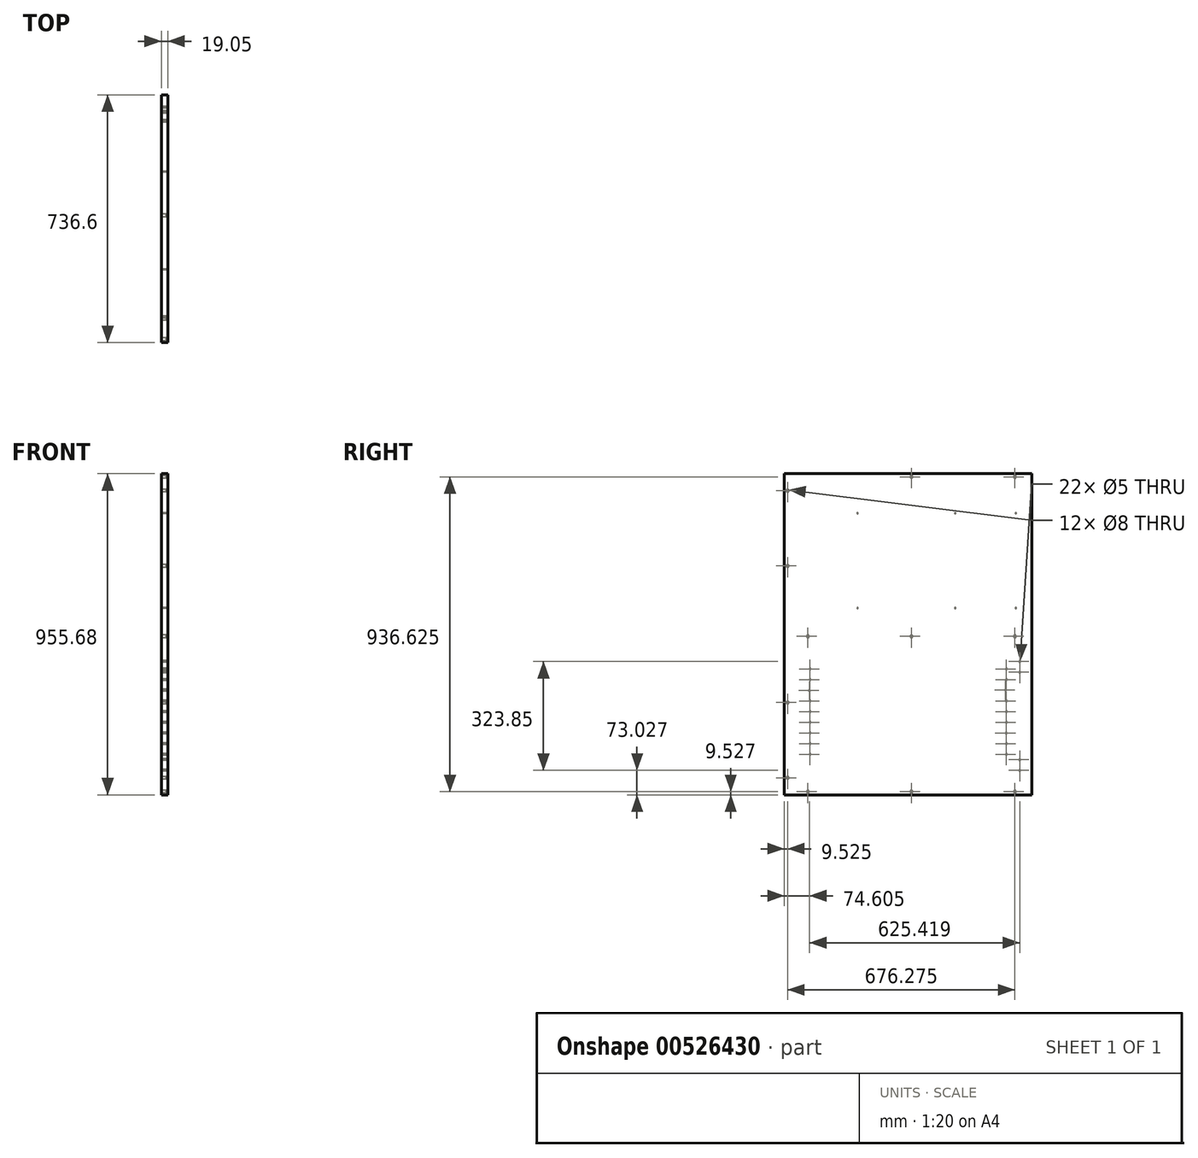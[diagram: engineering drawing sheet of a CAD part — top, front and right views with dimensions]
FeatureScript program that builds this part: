
annotation { "Feature Type Name" : "Feature", "Feature Type Description" : "" }
export const myFeature = defineFeature(function(context is Context, id is Id, definition is map)
    precondition{}
    {
        {
            var Q0;
            Q0=qCreatedBy(makeId("Right.planeOp"),FACE);
            var sketch = newSketch(context, id + "F0", { "sketchPlane" : qUnion([Q0])});
            skLineSegment(sketch, "E0.bottom", {"start": v(368.3, 477.84) * mm, "end": v(-368.3, 477.84) * mm});
            skLineSegment(sketch, "E0.top", {"start": v(368.3, -477.84) * mm, "end": v(-368.3, -477.84) * mm});
            skLineSegment(sketch, "E0.left", {"start": v(368.3, 477.84) * mm, "end": v(368.3, -477.84) * mm});
            skLineSegment(sketch, "E0.right", {"start": v(-368.3, 477.84) * mm, "end": v(-368.3, -477.84) * mm});
            skPoint(sketch, "E0.middle", {"position": v(0, 0) * mm});
            skSolve(sketch);
        }
        {
            var Q0;
            Q0=makeQuery(id+"F0.imprint","IMPRINT",FACE,{"disambiguationData":[TD([[makeQuery(id+"F0.imprint","IMPRINT",EDGE,{"derivedFrom":sQuery(id+"F0.wireOp",EDGE,"E0.bottom")}),1.0]])]});
            extrude(context, id + "F1", {"entities" : qUnion([Q0]), "depth" : 19.05 * mm, "offsetDistance" : 25.4 * mm});
        }
        {
            var Q0;
            Q0=makeQuery(id+"F1.opExtrude","CAP_FACE",FACE,{"disambiguationData":[OSD([sQuery(id+"F0.wireOp",EDGE,"E0.bottom"),sQuery(id+"F0.wireOp",EDGE,"E0.top"),sQuery(id+"F0.wireOp",EDGE,"E0.left"),sQuery(id+"F0.wireOp",EDGE,"E0.right")])],"isStart":false});
            var sketch = newSketch(context, id + "F2", { "sketchPlane" : qUnion([Q0])});
            skLineSegment(sketch, "E1", {"start": v(368.3, 477.84) * mm, "end": v(368.3, 468.31) * mm});
            skLineSegment(sketch, "E2", {"start": v(368.3, 468.31) * mm, "end": v(-368.3, 468.31) * mm});
            skLineSegment(sketch, "E3", {"start": v(-368.3, 477.84) * mm, "end": v(-349.25, 477.84) * mm});
            skLineSegment(sketch, "E4", {"start": v(-349.25, 477.84) * mm, "end": v(-349.25, -477.84) * mm});
            skLineSegment(sketch, "E5", {"start": v(-368.3, -477.84) * mm, "end": v(-368.3, -468.31) * mm});
            skLineSegment(sketch, "E6", {"start": v(-368.3, -468.31) * mm, "end": v(368.3, -468.31) * mm});
            skLineSegment(sketch, "E7", {"start": v(-368.3, -477.84) * mm, "end": v(-358.77, -477.84) * mm});
            skLineSegment(sketch, "E8", {"start": v(-358.77, -477.84) * mm, "end": v(-358.78, 477.84) * mm});
            skLineSegment(sketch, "E9", {"start": v(-368.3, 468.31) * mm, "end": v(-298.45, 468.31) * mm});
            skLineSegment(sketch, "E10", {"start": v(-368.3, -468.31) * mm, "end": v(-298.45, -468.31) * mm});
            skLineSegment(sketch, "E11", {"start": v(368.3, -468.31) * mm, "end": v(317.5, -468.31) * mm});
            skLineSegment(sketch, "E12", {"start": v(368.3, -468.31) * mm, "end": v(9.53, -468.31) * mm});
            skLineSegment(sketch, "E13", {"start": v(-358.78, 477.84) * mm, "end": v(-358.78, 427.04) * mm});
            skLineSegment(sketch, "E14", {"start": v(-358.77, -477.84) * mm, "end": v(-358.77, -427.04) * mm});
            skPoint(sketch, "E15", {"position": v(-358.78, 427.04) * mm});
            skPoint(sketch, "E16", {"position": v(317.5, -468.31) * mm});
            skPoint(sketch, "E17", {"position": v(9.53, -468.31) * mm});
            skPoint(sketch, "E18", {"position": v(-298.45, -468.31) * mm});
            skPoint(sketch, "E19", {"position": v(-358.77, -427.04) * mm});
            skPoint(sketch, "E20", {"position": v(-358.78, 0) * mm});
            skLineSegment(sketch, "E21", {"start": v(-368.3, 468.31) * mm, "end": v(-368.3, 477.84) * mm});
            skLineSegment(sketch, "E22", {"start": v(368.3, 468.31) * mm, "end": v(317.5, 468.31) * mm});
            skLineSegment(sketch, "E23", {"start": v(317.5, 468.31) * mm, "end": v(9.52, 468.31) * mm});
            skLineSegment(sketch, "E24", {"start": v(-358.78, 0) * mm, "end": v(-358.78, 203.2) * mm});
            skLineSegment(sketch, "E25", {"start": v(-358.78, 203.2) * mm, "end": v(-358.77, -203.2) * mm});
            skPoint(sketch, "E26", {"position": v(-358.78, 203.2) * mm});
            skPoint(sketch, "E27", {"position": v(-358.77, -203.2) * mm});
            skSolve(sketch);
        }
        {
            var Q0;
            Q0=sQuery(id+"F2.wireOp",VERTEX,"E9.end");
            var Q1;
            Q1=sQuery(id+"F2.wireOp",VERTEX,"E23.end");
            var Q2;
            Q2=sQuery(id+"F2.wireOp",VERTEX,"E23.start");
            var Q3;
            Q3=sQuery(id+"F2.wireOp",VERTEX,"E15");
            var Q4;
            Q4=sQuery(id+"F2.wireOp",VERTEX,"E19");
            var Q5;
            Q5=sQuery(id+"F2.wireOp",VERTEX,"E18");
            var Q6;
            Q6=sQuery(id+"F2.wireOp",VERTEX,"E17");
            var Q7;
            Q7=sQuery(id+"F2.wireOp",VERTEX,"E16");
            var Q8;
            Q8=sQuery(id+"F2.wireOp",VERTEX,"E26");
            var Q9;
            Q9=sQuery(id+"F2.wireOp",VERTEX,"E27");
            var Q10;
            Q10=makeQuery(id+"F1.opExtrude","SWEPT_BODY",BODY,{"disambiguationData":[OSD([sQuery(id+"F0.wireOp",EDGE,"E0.bottom"),sQuery(id+"F0.wireOp",EDGE,"E0.top"),sQuery(id+"F0.wireOp",EDGE,"E0.left"),sQuery(id+"F0.wireOp",EDGE,"E0.right")])]});
            hole(context, id + "F3", {"style" : HoleStyle.SIMPLE, "endStyle" : HoleEndStyle.BLIND, "holeDiameter" : 8 * mm, "holeDepth" : 14.22 * mm, "isTappedThrough" : true, "tappedDepth" : 12.7 * mm, "tapClearance" : 3, "startFromSketch" : true, "locations" : qUnion([Q0, Q1, Q2, Q3, Q4, Q5, Q6, Q7, Q8, Q9]), "scope" : qUnion([Q10])});
        }
        {
            var Q0;
            Q0=makeQuery(id+"F1.opExtrude","CAP_FACE",FACE,{"disambiguationData":[OSD([sQuery(id+"F0.wireOp",EDGE,"E0.bottom"),sQuery(id+"F0.wireOp",EDGE,"E0.top"),sQuery(id+"F0.wireOp",EDGE,"E0.left"),sQuery(id+"F0.wireOp",EDGE,"E0.right")])],"isStart":false});
            var sketch = newSketch(context, id + "F4", { "sketchPlane" : qUnion([Q0])});
            skLineSegment(sketch, "E28", {"start": v(368.3, 477.84) * mm, "end": v(368.3, 363.54) * mm});
            skLineSegment(sketch, "E29", {"start": v(368.3, 477.84) * mm, "end": v(368.3, 458.79) * mm});
            skLineSegment(sketch, "E30", {"start": v(368.3, 458.79) * mm, "end": v(368.3, 360.24) * mm});
            skLineSegment(sketch, "E31", {"start": v(368.3, 360.24) * mm, "end": v(-241.3, 360.24) * mm});
            skLineSegment(sketch, "E32", {"start": v(368.3, 360.24) * mm, "end": v(320.04, 360.24) * mm});
            skLineSegment(sketch, "E33", {"start": v(368.3, 360.24) * mm, "end": v(139.7, 360.24) * mm});
            skLineSegment(sketch, "E34", {"start": v(368.3, 360.24) * mm, "end": v(-150.88, 360.24) * mm});
            skPoint(sketch, "E35", {"position": v(320.04, 360.24) * mm});
            skPoint(sketch, "E36", {"position": v(139.7, 360.24) * mm});
            skPoint(sketch, "E37", {"position": v(-150.88, 360.24) * mm});
            skLineSegment(sketch, "E38", {"start": v(368.3, 477.84) * mm, "end": v(368.3, 468.31) * mm});
            skLineSegment(sketch, "E39", {"start": v(368.3, 468.31) * mm, "end": v(387.35, 468.31) * mm});
            skLineSegment(sketch, "E40", {"start": v(387.35, 468.31) * mm, "end": v(387.35, 303.21) * mm});
            skLineSegment(sketch, "E41", {"start": v(387.35, 303.21) * mm, "end": v(368.3, 303.21) * mm});
            skLineSegment(sketch, "E42", {"start": v(368.3, 303.21) * mm, "end": v(368.3, 300.04) * mm});
            skLineSegment(sketch, "E43", {"start": v(368.3, 300.04) * mm, "end": v(387.35, 300.04) * mm});
            skLineSegment(sketch, "E44", {"start": v(387.35, 300.04) * mm, "end": v(387.35, 0) * mm});
            skLineSegment(sketch, "E45", {"start": v(387.35, 300.04) * mm, "end": v(387.35, -4.76) * mm});
            skLineSegment(sketch, "E46", {"start": v(387.35, -4.76) * mm, "end": v(368.3, -4.76) * mm});
            skLineSegment(sketch, "E47", {"start": v(368.3, -4.76) * mm, "end": v(368.3, -7.94) * mm});
            skLineSegment(sketch, "E48", {"start": v(368.3, -7.94) * mm, "end": v(387.35, -7.94) * mm});
            skLineSegment(sketch, "E49", {"start": v(387.35, -7.94) * mm, "end": v(387.35, -477.84) * mm});
            skLineSegment(sketch, "E50", {"start": v(387.35, -477.84) * mm, "end": v(368.3, -477.84) * mm});
            skLineSegment(sketch, "E51", {"start": v(387.35, 147.64) * mm, "end": v(387.35, 280.99) * mm});
            skLineSegment(sketch, "E52", {"start": v(387.35, 280.99) * mm, "end": v(311.15, 280.99) * mm});
            skLineSegment(sketch, "E53", {"start": v(311.15, 280.99) * mm, "end": v(311.15, 14.29) * mm});
            skLineSegment(sketch, "E54", {"start": v(311.15, 14.29) * mm, "end": v(387.35, 14.29) * mm});
            skLineSegment(sketch, "E55", {"start": v(368.3, 14.29) * mm, "end": v(368.3, 77.79) * mm});
            skLineSegment(sketch, "E56", {"start": v(368.3, 77.79) * mm, "end": v(-241.3, 77.79) * mm});
            skLineSegment(sketch, "E57", {"start": v(368.3, 77.79) * mm, "end": v(320.04, 77.79) * mm});
            skLineSegment(sketch, "E58", {"start": v(368.3, 77.79) * mm, "end": v(-150.88, 77.79) * mm});
            skLineSegment(sketch, "E59", {"start": v(368.3, 77.79) * mm, "end": v(139.7, 77.79) * mm});
            skPoint(sketch, "E60", {"position": v(139.7, 77.79) * mm});
            skPoint(sketch, "E61", {"position": v(-150.88, 77.79) * mm});
            skPoint(sketch, "E62", {"position": v(320.04, 77.79) * mm});
            skLineSegment(sketch, "E63", {"start": v(368.3, -6.35) * mm, "end": v(-368.3, -6.35) * mm});
            skLineSegment(sketch, "E64", {"start": v(-368.3, -6.35) * mm, "end": v(-298.45, -6.35) * mm});
            skLineSegment(sketch, "E65", {"start": v(368.3, -6.35) * mm, "end": v(317.5, -6.35) * mm});
            skLineSegment(sketch, "E66", {"start": v(368.3, -6.35) * mm, "end": v(9.52, -6.35) * mm});
            skPoint(sketch, "E67", {"position": v(317.5, -6.35) * mm});
            skPoint(sketch, "E68", {"position": v(9.52, -6.35) * mm});
            skPoint(sketch, "E69", {"position": v(-298.45, -6.35) * mm});
            skSolve(sketch);
        }
        {
            var Q0;
            Q0=sQuery(id+"F4.wireOp",VERTEX,"E37");
            var Q1;
            Q1=sQuery(id+"F4.wireOp",VERTEX,"E36");
            var Q2;
            Q2=sQuery(id+"F4.wireOp",VERTEX,"E35");
            var Q3;
            Q3=sQuery(id+"F4.wireOp",VERTEX,"E62");
            var Q4;
            Q4=sQuery(id+"F4.wireOp",VERTEX,"E60");
            var Q5;
            Q5=sQuery(id+"F4.wireOp",VERTEX,"E61");
            var Q6;
            Q6=makeQuery(id+"F1.opExtrude","SWEPT_BODY",BODY,{"disambiguationData":[OSD([sQuery(id+"F0.wireOp",EDGE,"E0.bottom"),sQuery(id+"F0.wireOp",EDGE,"E0.top"),sQuery(id+"F0.wireOp",EDGE,"E0.left"),sQuery(id+"F0.wireOp",EDGE,"E0.right")])]});
            hole(context, id + "F5", {"style" : HoleStyle.SIMPLE, "endStyle" : HoleEndStyle.BLIND, "holeDiameter" : 3.17 * mm, "holeDepth" : 14.22 * mm, "isTappedThrough" : true, "tappedDepth" : 12.7 * mm, "tapClearance" : 3, "startFromSketch" : true, "locations" : qUnion([Q0, Q1, Q2, Q3, Q4, Q5]), "scope" : qUnion([Q6])});
        }
        {
            var Q0;
            Q0=sQuery(id+"F4.wireOp",VERTEX,"E69");
            var Q1;
            Q1=sQuery(id+"F4.wireOp",VERTEX,"E68");
            var Q2;
            Q2=sQuery(id+"F4.wireOp",VERTEX,"E67");
            var Q3;
            Q3=makeQuery(id+"F1.opExtrude","SWEPT_BODY",BODY,{"disambiguationData":[OSD([sQuery(id+"F0.wireOp",EDGE,"E0.bottom"),sQuery(id+"F0.wireOp",EDGE,"E0.top"),sQuery(id+"F0.wireOp",EDGE,"E0.left"),sQuery(id+"F0.wireOp",EDGE,"E0.right")])]});
            hole(context, id + "F6", {"style" : HoleStyle.SIMPLE, "endStyle" : HoleEndStyle.BLIND, "holeDiameter" : 8 * mm, "holeDepth" : 14.22 * mm, "isTappedThrough" : true, "tappedDepth" : 12.7 * mm, "tapClearance" : 3, "startFromSketch" : true, "locations" : qUnion([Q0, Q1, Q2]), "scope" : qUnion([Q3])});
        }
        {
            var Q0;
            Q0=makeQuery(id+"F1.opExtrude","CAP_FACE",FACE,{"disambiguationData":[OSD([sQuery(id+"F0.wireOp",EDGE,"E0.bottom"),sQuery(id+"F0.wireOp",EDGE,"E0.top"),sQuery(id+"F0.wireOp",EDGE,"E0.left"),sQuery(id+"F0.wireOp",EDGE,"E0.right")])],"isStart":false});
            var sketch = newSketch(context, id + "F7", { "sketchPlane" : qUnion([Q0])});
            skLineSegment(sketch, "E70", {"start": v(368.3, -477.84) * mm, "end": v(292.1, -477.84) * mm});
            skLineSegment(sketch, "E71", {"start": v(292.1, -477.84) * mm, "end": v(292.1, -46.04) * mm});
            skLineSegment(sketch, "E72", {"start": v(-368.3, -477.84) * mm, "end": v(-292.1, -477.84) * mm});
            skLineSegment(sketch, "E73", {"start": v(-292.1, -477.84) * mm, "end": v(-292.1, -46.04) * mm});
            skLineSegment(sketch, "E74", {"start": v(292.1, -477.84) * mm, "end": v(292.1, -325.44) * mm});
            skLineSegment(sketch, "E75", {"start": v(-292.1, -477.84) * mm, "end": v(-292.1, -325.44) * mm});
            skLineSegment(sketch, "E76", {"start": v(-292.1, -325.44) * mm, "end": v(-292.1, -293.69) * mm});
            skLineSegment(sketch, "E77", {"start": v(-292.1, -293.69) * mm, "end": v(-292.1, -261.94) * mm});
            skLineSegment(sketch, "E78", {"start": v(-292.1, -261.94) * mm, "end": v(-292.1, -230.19) * mm});
            skLineSegment(sketch, "E79", {"start": v(-292.1, -230.19) * mm, "end": v(-292.1, -198.44) * mm});
            skLineSegment(sketch, "E80", {"start": v(-292.1, -198.44) * mm, "end": v(-292.1, -166.69) * mm});
            skLineSegment(sketch, "E81", {"start": v(-292.1, -166.69) * mm, "end": v(-292.1, -134.94) * mm});
            skLineSegment(sketch, "E82", {"start": v(-292.1, -134.94) * mm, "end": v(-292.1, -103.19) * mm});
            skLineSegment(sketch, "E83", {"start": v(-292.1, -325.44) * mm, "end": v(-292.1, -357.19) * mm});
            skLineSegment(sketch, "E84", {"start": v(-292.1, -357.19) * mm, "end": v(-292.1, -477.84) * mm});
            skLineSegment(sketch, "E85", {"start": v(292.1, -477.84) * mm, "end": v(292.1, -357.19) * mm});
            skLineSegment(sketch, "E86", {"start": v(292.1, -325.44) * mm, "end": v(292.1, -293.69) * mm});
            skLineSegment(sketch, "E87", {"start": v(292.1, -293.69) * mm, "end": v(292.1, -261.94) * mm});
            skLineSegment(sketch, "E88", {"start": v(292.1, -261.94) * mm, "end": v(292.1, -230.19) * mm});
            skLineSegment(sketch, "E89", {"start": v(292.1, -230.19) * mm, "end": v(292.1, -198.44) * mm});
            skLineSegment(sketch, "E90", {"start": v(292.1, -198.44) * mm, "end": v(292.1, -166.69) * mm});
            skLineSegment(sketch, "E91", {"start": v(292.1, -166.69) * mm, "end": v(292.1, -134.94) * mm});
            skLineSegment(sketch, "E92", {"start": v(292.1, -134.94) * mm, "end": v(292.1, -103.19) * mm});
            skPoint(sketch, "E93", {"position": v(-292.1, -103.19) * mm});
            skPoint(sketch, "E94", {"position": v(-292.1, -134.94) * mm});
            skPoint(sketch, "E95", {"position": v(-293.7, -167.67) * mm});
            skPoint(sketch, "E96", {"position": v(-292.1, -198.44) * mm});
            skPoint(sketch, "E97", {"position": v(-292.1, -230.19) * mm});
            skPoint(sketch, "E98", {"position": v(-292.1, -261.94) * mm});
            skPoint(sketch, "E99", {"position": v(-292.1, -293.69) * mm});
            skPoint(sketch, "E100", {"position": v(-292.1, -325.44) * mm});
            skPoint(sketch, "E101", {"position": v(-292.1, -357.19) * mm});
            skPoint(sketch, "E102", {"position": v(292.1, -357.19) * mm});
            skPoint(sketch, "E103", {"position": v(292.1, -325.44) * mm});
            skPoint(sketch, "E104", {"position": v(291.52, -294.05) * mm});
            skPoint(sketch, "E105", {"position": v(292.1, -261.94) * mm});
            skPoint(sketch, "E106", {"position": v(292.1, -230.19) * mm});
            skPoint(sketch, "E107", {"position": v(292.1, -198.44) * mm});
            skPoint(sketch, "E108", {"position": v(289.58, -165.73) * mm});
            skPoint(sketch, "E109", {"position": v(292.1, -134.94) * mm});
            skPoint(sketch, "E110", {"position": v(292.1, -103.19) * mm});
            skSolve(sketch);
        }
        {
            var Q0;
            Q0=sQuery(id+"F7.wireOp",VERTEX,"E93");
            var Q1;
            Q1=sQuery(id+"F7.wireOp",VERTEX,"E94");
            var Q2;
            Q2=sQuery(id+"F7.wireOp",VERTEX,"E95");
            var Q3;
            Q3=sQuery(id+"F7.wireOp",VERTEX,"E96");
            var Q4;
            Q4=sQuery(id+"F7.wireOp",VERTEX,"E97");
            var Q5;
            Q5=sQuery(id+"F7.wireOp",VERTEX,"E98");
            var Q6;
            Q6=sQuery(id+"F7.wireOp",VERTEX,"E99");
            var Q7;
            Q7=sQuery(id+"F7.wireOp",VERTEX,"E100");
            var Q8;
            Q8=sQuery(id+"F7.wireOp",VERTEX,"E101");
            var Q9;
            Q9=sQuery(id+"F7.wireOp",VERTEX,"E102");
            var Q10;
            Q10=sQuery(id+"F7.wireOp",VERTEX,"E103");
            var Q11;
            Q11=sQuery(id+"F7.wireOp",VERTEX,"E104");
            var Q12;
            Q12=sQuery(id+"F7.wireOp",VERTEX,"E105");
            var Q13;
            Q13=sQuery(id+"F7.wireOp",VERTEX,"E106");
            var Q14;
            Q14=sQuery(id+"F7.wireOp",VERTEX,"E107");
            var Q15;
            Q15=sQuery(id+"F7.wireOp",VERTEX,"E108");
            var Q16;
            Q16=sQuery(id+"F7.wireOp",VERTEX,"E109");
            var Q17;
            Q17=sQuery(id+"F7.wireOp",VERTEX,"E110");
            var Q18;
            Q18=makeQuery(id+"F1.opExtrude","SWEPT_BODY",BODY,{"disambiguationData":[OSD([sQuery(id+"F0.wireOp",EDGE,"E0.bottom"),sQuery(id+"F0.wireOp",EDGE,"E0.top"),sQuery(id+"F0.wireOp",EDGE,"E0.left"),sQuery(id+"F0.wireOp",EDGE,"E0.right")])]});
            hole(context, id + "F8", {"style" : HoleStyle.SIMPLE, "endStyle" : HoleEndStyle.BLIND, "holeDiameter" : 5 * mm, "holeDepth" : 14.22 * mm, "isTappedThrough" : true, "tappedDepth" : 12.7 * mm, "tapClearance" : 3, "startFromSketch" : true, "locations" : qUnion([Q0, Q1, Q2, Q3, Q4, Q5, Q6, Q7, Q8, Q9, Q10, Q11, Q12, Q13, Q14, Q15, Q16, Q17]), "scope" : qUnion([Q18])});
        }
        {
            var Q0;
            Q0=makeQuery(id+"F1.opExtrude","SWEPT_BODY",BODY,{"disambiguationData":[OSD([sQuery(id+"F0.wireOp",EDGE,"E0.bottom"),sQuery(id+"F0.wireOp",EDGE,"E0.top"),sQuery(id+"F0.wireOp",EDGE,"E0.left"),sQuery(id+"F0.wireOp",EDGE,"E0.right")])]});
            var Q1;
            Q1=makeQuery(id+"F1.opExtrude","CAP_FACE",FACE,{"disambiguationData":[OSD([sQuery(id+"F0.wireOp",EDGE,"E0.bottom"),sQuery(id+"F0.wireOp",EDGE,"E0.top"),sQuery(id+"F0.wireOp",EDGE,"E0.left"),sQuery(id+"F0.wireOp",EDGE,"E0.right")])],"isStart":false});
            mirror(context, id + "F9", {"entities" : qUnion([Q0]), "mirrorPlane" : qUnion([Q1])});
        }
        {
            var Q0;
            Q0=makeQuery(id+"F1.opExtrude","SWEPT_BODY",BODY,{"disambiguationData":[OSD([sQuery(id+"F0.wireOp",EDGE,"E0.bottom"),sQuery(id+"F0.wireOp",EDGE,"E0.top"),sQuery(id+"F0.wireOp",EDGE,"E0.left"),sQuery(id+"F0.wireOp",EDGE,"E0.right")])]});
            deleteBodies(context, id + "F10", {"entities" : qUnion([Q0])});
        }
        {
            var Q0;
            Q0=makeQuery(id+"F9.opPattern","COPY",FACE,{"derivedFrom":makeQuery(id+"F1.opExtrude","CAP_FACE",FACE,{"disambiguationData":[OSD([sQuery(id+"F0.wireOp",EDGE,"E0.bottom"),sQuery(id+"F0.wireOp",EDGE,"E0.top"),sQuery(id+"F0.wireOp",EDGE,"E0.left"),sQuery(id+"F0.wireOp",EDGE,"E0.right")])],"isStart":false}),"instanceName":"1"});
            var sketch = newSketch(context, id + "F11", { "sketchPlane" : qUnion([Q0])});
            skLineSegment(sketch, "E111", {"start": v(-368.3, -477.84) * mm, "end": v(-368.3, -7.94) * mm});
            skLineSegment(sketch, "E112", {"start": v(-368.3, -7.94) * mm, "end": v(-387.35, -7.94) * mm});
            skLineSegment(sketch, "E113", {"start": v(-387.35, -7.94) * mm, "end": v(-387.35, -477.84) * mm});
            skLineSegment(sketch, "E114", {"start": v(-387.35, -477.84) * mm, "end": v(-368.3, -477.84) * mm});
            skLineSegment(sketch, "E115", {"start": v(-368.3, -477.84) * mm, "end": v(-368.3, -388.94) * mm});
            skLineSegment(sketch, "E116", {"start": v(-368.3, -388.94) * mm, "end": v(-331.72, -388.94) * mm});
            skLineSegment(sketch, "E117", {"start": v(-331.72, -388.94) * mm, "end": v(-331.72, -404.81) * mm});
            skLineSegment(sketch, "E118", {"start": v(-331.72, -404.81) * mm, "end": v(-331.72, -373.06) * mm});
            skPoint(sketch, "E119", {"position": v(-331.72, -373.06) * mm});
            skPoint(sketch, "E120", {"position": v(-331.72, -404.81) * mm});
            skLineSegment(sketch, "E121", {"start": v(-368.3, -7.94) * mm, "end": v(-368.3, -96.84) * mm});
            skLineSegment(sketch, "E122", {"start": v(-368.3, -96.84) * mm, "end": v(-331.72, -96.84) * mm});
            skLineSegment(sketch, "E123", {"start": v(-331.72, -96.84) * mm, "end": v(-331.72, -112.71) * mm});
            skLineSegment(sketch, "E124", {"start": v(-331.72, -112.71) * mm, "end": v(-331.72, -80.96) * mm});
            skPoint(sketch, "E125", {"position": v(-331.72, -80.96) * mm});
            skPoint(sketch, "E126", {"position": v(-331.72, -112.71) * mm});
            skSolve(sketch);
        }
        {
            var Q0;
            Q0=sQuery(id+"F11.wireOp",VERTEX,"E125");
            var Q1;
            Q1=sQuery(id+"F11.wireOp",VERTEX,"E126");
            var Q2;
            Q2=sQuery(id+"F11.wireOp",VERTEX,"E119");
            var Q3;
            Q3=sQuery(id+"F11.wireOp",VERTEX,"E120");
            var Q4;
            Q4=makeQuery(id+"F9.opPattern","COPY",BODY,{"derivedFrom":makeQuery(id+"F1.opExtrude","SWEPT_BODY",BODY,{"disambiguationData":[OSD([sQuery(id+"F0.wireOp",EDGE,"E0.bottom"),sQuery(id+"F0.wireOp",EDGE,"E0.top"),sQuery(id+"F0.wireOp",EDGE,"E0.left"),sQuery(id+"F0.wireOp",EDGE,"E0.right")])]}),"instanceName":"1"});
            hole(context, id + "F12", {"style" : HoleStyle.SIMPLE, "endStyle" : HoleEndStyle.BLIND, "holeDiameter" : 5 * mm, "holeDepth" : 14.22 * mm, "isTappedThrough" : true, "tappedDepth" : 12.7 * mm, "tapClearance" : 3, "startFromSketch" : true, "locations" : qUnion([Q0, Q1, Q2, Q3]), "scope" : qUnion([Q4])});
        }
    });
